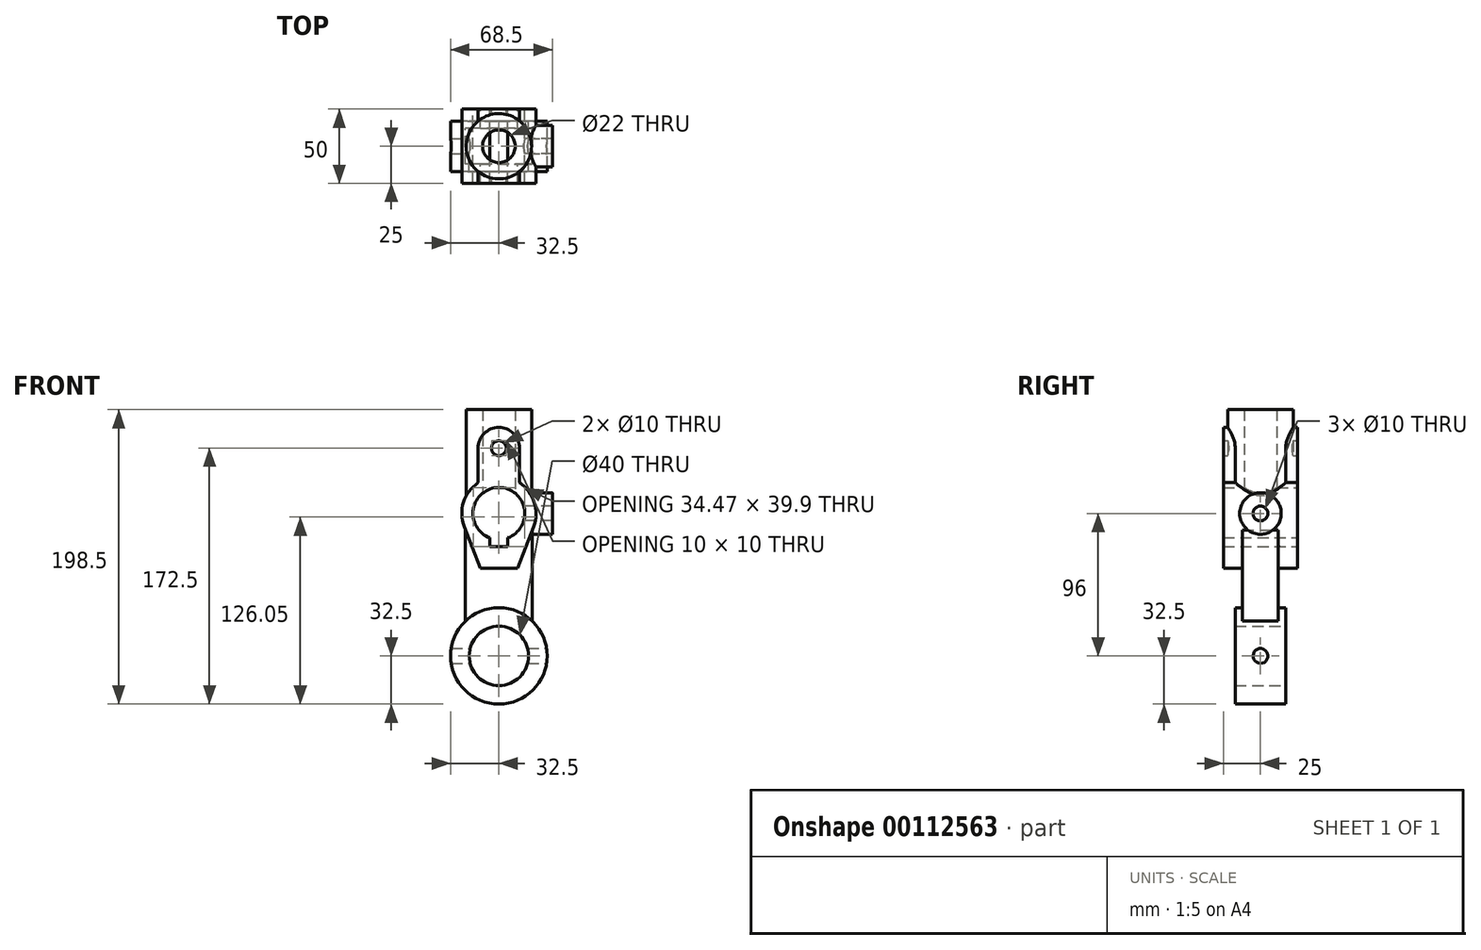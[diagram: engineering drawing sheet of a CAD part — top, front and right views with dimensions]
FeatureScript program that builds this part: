
annotation { "Feature Type Name" : "Feature", "Feature Type Description" : "" }
export const myFeature = defineFeature(function(context is Context, id is Id, definition is map)
    precondition{}
    {
        {
            var Q0;
            Q0=qCreatedBy(makeId("Front.planeOp"),FACE);
            var sketch = newSketch(context, id + "F0", { "sketchPlane" : qUnion([Q0])});
            skCircle(sketch, "E0", {"center": v(0, 0) * mm, "radius": 20 * mm});
            skCircle(sketch, "E1", {"center": v(0, 0) * mm, "radius": 32.5 * mm});
            skArc(sketch, "E2", {"start": v(6, 79.56) * mm, "mid": v(0, 113.5) * mm, "end": v(-6, 79.56) * mm});
            skLineSegment(sketch, "E3", {"start": v(-6, 79.56) * mm, "end": v(-6, 73.6) * mm});
            skLineSegment(sketch, "E4", {"start": v(6, 73.6) * mm, "end": v(6, 79.56) * mm});
            skPoint(sketch, "E5", {"position": v(0, 78.5) * mm});
            skLineSegment(sketch, "E6", {"start": v(-6, 73.6) * mm, "end": v(6, 73.6) * mm});
            skPoint(sketch, "E7", {"position": v(0, 113.5) * mm});
            skArc(sketch, "E8", {"start": v(23.32, 86.98) * mm, "mid": v(23.86, 103.48) * mm, "end": v(14, 116.71) * mm});
            skLineSegment(sketch, "E9", {"start": v(-12.5, 59) * mm, "end": v(12.5, 59) * mm});
            skLineSegment(sketch, "E10", {"start": v(12.5, 59) * mm, "end": v(23.32, 86.98) * mm});
            skLineSegment(sketch, "E11", {"start": v(-12.5, 59) * mm, "end": v(-23.32, 86.98) * mm});
            skLineSegment(sketch, "E12", {"start": v(-22.5, 23.45) * mm, "end": v(-22.5, 84.87) * mm});
            skLineSegment(sketch, "E13", {"start": v(22.5, 23.45) * mm, "end": v(22.5, 84.87) * mm});
            skPoint(sketch, "E14", {"position": v(0, 32.5) * mm});
            skCircle(sketch, "E15", {"center": v(0, 140) * mm, "radius": 5 * mm});
            skPoint(sketch, "E15.centerSnap0", {"position": v(0, 121) * mm});
            skArc(sketch, "E16", {"start": v(14, 140) * mm, "mid": v(0, 154) * mm, "end": v(-14, 140) * mm});
            skLineSegment(sketch, "E17", {"start": v(-14, 140) * mm, "end": v(-14, 116.71) * mm});
            skLineSegment(sketch, "E18", {"start": v(14, 140) * mm, "end": v(14, 116.71) * mm});
            skArc(sketch, "E19.trimOffspring", {"start": v(-14, 116.71) * mm, "mid": v(-23.86, 103.48) * mm, "end": v(-23.32, 86.98) * mm});
            skSolve(sketch);
        }
        {
            var Q0;
            Q0=makeQuery(id+"F0.imprint","IMPRINT",FACE,{"disambiguationData":[TD([[makeQuery(id+"F0.imprint","IMPRINT",EDGE,{"derivedFrom":sQuery(id+"F0.wireOp",EDGE,"E0")}),-1.0]])]});
            extrude(context, id + "F1", {"entities" : qUnion([Q0]), "endBound" : BoundingType.SYMMETRIC, "depth" : 34 * mm});
        }
        {
            var Q0;
            {var subQ1=sQuery(id+"F0.wireOp",EDGE,"E9");Q0=makeQuery(id+"F0.imprint","IMPRINT",FACE,{"disambiguationData":[TD([[makeQuery(id+"F0.imprint","IMPRINT",EDGE,{"derivedFrom":subQ1}),-1.0]])]});}
            extrude(context, id + "F2", {"entities" : qUnion([Q0]), "operationType" : NewBodyOperationType.ADD, "endBound" : BoundingType.SYMMETRIC, "depth" : 24 * mm});
        }
        {
            var Q0;
            Q0=makeQuery(id+"F0.imprint","IMPRINT",FACE,{"disambiguationData":[TD([[makeQuery(id+"F0.imprint","IMPRINT",EDGE,{"derivedFrom":sQuery(id+"F0.wireOp",EDGE,"E2")}),-1.0]])]});
            extrude(context, id + "F3", {"entities" : qUnion([Q0]), "operationType" : NewBodyOperationType.ADD, "endBound" : BoundingType.SYMMETRIC, "depth" : 50 * mm});
        }
        {
            var Q0;
            Q0=makeQuery(id+"F3.opExtrude","SWEPT_FACE",FACE,{"disambiguationData":[OSD([sQuery(id+"F0.wireOp",EDGE,"E6")])]});
            var sketch = newSketch(context, id + "F4", { "sketchPlane" : qUnion([Q0])});
            skCircle(sketch, "E20", {"center": v(0, 0) * mm, "radius": 11 * mm});
            skCircle(sketch, "E21", {"center": v(0, 0) * mm, "radius": 22 * mm});
            skSolve(sketch);
        }
        {
            var Q0;
            Q0 = qSketchRegion(id + "F4", true);
            extrude(context, id + "F5", {"entities" : qUnion([Q0]), "operationType" : NewBodyOperationType.ADD, "depth" : 92.4 * mm});
        }
        {
            var Q0;
            Q0=makeQuery(id+"F3.opExtrude","CAP_FACE",FACE,{"disambiguationData":[OSD([sQuery(id+"F0.wireOp",EDGE,"E2"),sQuery(id+"F0.wireOp",EDGE,"E3"),sQuery(id+"F0.wireOp",EDGE,"E4"),sQuery(id+"F0.wireOp",EDGE,"E6"),sQuery(id+"F0.wireOp",EDGE,"E8"),sQuery(id+"F0.wireOp",EDGE,"E9"),sQuery(id+"F0.wireOp",EDGE,"E10"),sQuery(id+"F0.wireOp",EDGE,"E11"),sQuery(id+"F0.wireOp",EDGE,"E15"),sQuery(id+"F0.wireOp",EDGE,"E16"),sQuery(id+"F0.wireOp",EDGE,"E17"),sQuery(id+"F0.wireOp",EDGE,"E18"),sQuery(id+"F0.wireOp",EDGE,"E19.trimOffspring")])],"isStart":false});
            var sketch = newSketch(context, id + "F6", { "sketchPlane" : qUnion([Q0])});
            skSolve(sketch);
        }
        {
            var Q0;
            Q0=qCreatedBy(makeId("Right.planeOp"),FACE);
            var sketch = newSketch(context, id + "F7", { "sketchPlane" : qUnion([Q0])});
            skLineSegment(sketch, "E22", {"start": v(0, 0) * mm, "end": v(0, 96) * mm});
            skCircle(sketch, "E23", {"center": v(0, 96) * mm, "radius": 5 * mm});
            skCircle(sketch, "E24", {"center": v(0, 96) * mm, "radius": 14 * mm});
            skSolve(sketch);
        }
        {
            var Q0;
            Q0=makeQuery(id+"F7.imprint","IMPRINT",FACE,{"disambiguationData":[TD([[makeQuery(id+"F7.imprint","IMPRINT",EDGE,{"derivedFrom":sQuery(id+"F7.wireOp",EDGE,"E23")}),-1.0]])]});
            extrude(context, id + "F8", {"entities" : qUnion([Q0]), "operationType" : NewBodyOperationType.ADD, "depth" : 36 * mm});
        }
        {
            var Q0;
            Q0=makeQuery(id+"F6.imprint","IMPRINT",FACE,{"disambiguationData":[TD([[makeQuery(id+"F6.imprint","IMPRINT",EDGE,{"derivedFrom":makeQuery(id+"F3.opExtrude","CAP_EDGE",EDGE,{"disambiguationData":[OSD([sQuery(id+"F0.wireOp",EDGE,"E2")])],"isStart":false})}),1.0]])]});
            extrude(context, id + "F9", {"entities" : qUnion([Q0]), "operationType" : NewBodyOperationType.REMOVE, "endBound" : BoundingType.THROUGH_ALL, "oppositeDirection" : true, "depth" : 25 * mm});
        }
        {
            var Q0;
            Q0=makeQuery(id+"F8.opExtrude","CAP_FACE",FACE,{"disambiguationData":[OSD([sQuery(id+"F7.wireOp",EDGE,"E23"),sQuery(id+"F7.wireOp",EDGE,"E24")])],"isStart":false});
            var sketch = newSketch(context, id + "F10", { "sketchPlane" : qUnion([Q0])});
            skSolve(sketch);
        }
        {
            var Q0;
            Q0=makeQuery(id+"F10.imprint","IMPRINT",FACE,{"disambiguationData":[TD([[makeQuery(id+"F10.imprint","IMPRINT",EDGE,{"derivedFrom":makeQuery(id+"F8.opExtrude","CAP_EDGE",EDGE,{"disambiguationData":[OSD([sQuery(id+"F7.wireOp",EDGE,"E23")])],"isStart":false})}),1.0]])]});
            extrude(context, id + "F11", {"entities" : qUnion([Q0]), "operationType" : NewBodyOperationType.REMOVE, "oppositeDirection" : true, "depth" : 36 * mm});
        }
        {
            var Q0;
            Q0=qCreatedBy(makeId("Right.planeOp"),FACE);
            var sketch = newSketch(context, id + "F12", { "sketchPlane" : qUnion([Q0])});
            skCircle(sketch, "E25", {"center": v(0, 0) * mm, "radius": 5 * mm});
            skSolve(sketch);
        }
        {
            var Q0;
            Q0 = qSketchRegion(id + "F12", true);
            extrude(context, id + "F13", {"entities" : qUnion([Q0]), "operationType" : NewBodyOperationType.REMOVE, "endBound" : BoundingType.SYMMETRIC, "oppositeDirection" : true, "depth" : 100 * mm});
        }
        {
            var Q0;
            Q0=makeQuery(id+"F5.opExtrude","CAP_FACE",FACE,{"disambiguationData":[OSD([sQuery(id+"F4.wireOp",EDGE,"E20"),sQuery(id+"F4.wireOp",EDGE,"E21")])],"isStart":false});
            var sketch = newSketch(context, id + "F14", { "sketchPlane" : qUnion([Q0])});
            skSolve(sketch);
        }
        {
            var Q0;
            Q0=makeQuery(id+"F14.imprint","IMPRINT",FACE,{"disambiguationData":[TD([[makeQuery(id+"F14.imprint","IMPRINT",EDGE,{"derivedFrom":makeQuery(id+"F5.opExtrude","CAP_EDGE",EDGE,{"disambiguationData":[OSD([sQuery(id+"F4.wireOp",EDGE,"E20")])],"isStart":false})}),1.0]])]});
            extrude(context, id + "F15", {"entities" : qUnion([Q0]), "operationType" : NewBodyOperationType.REMOVE, "oppositeDirection" : true, "depth" : 60 * mm});
        }
    });
